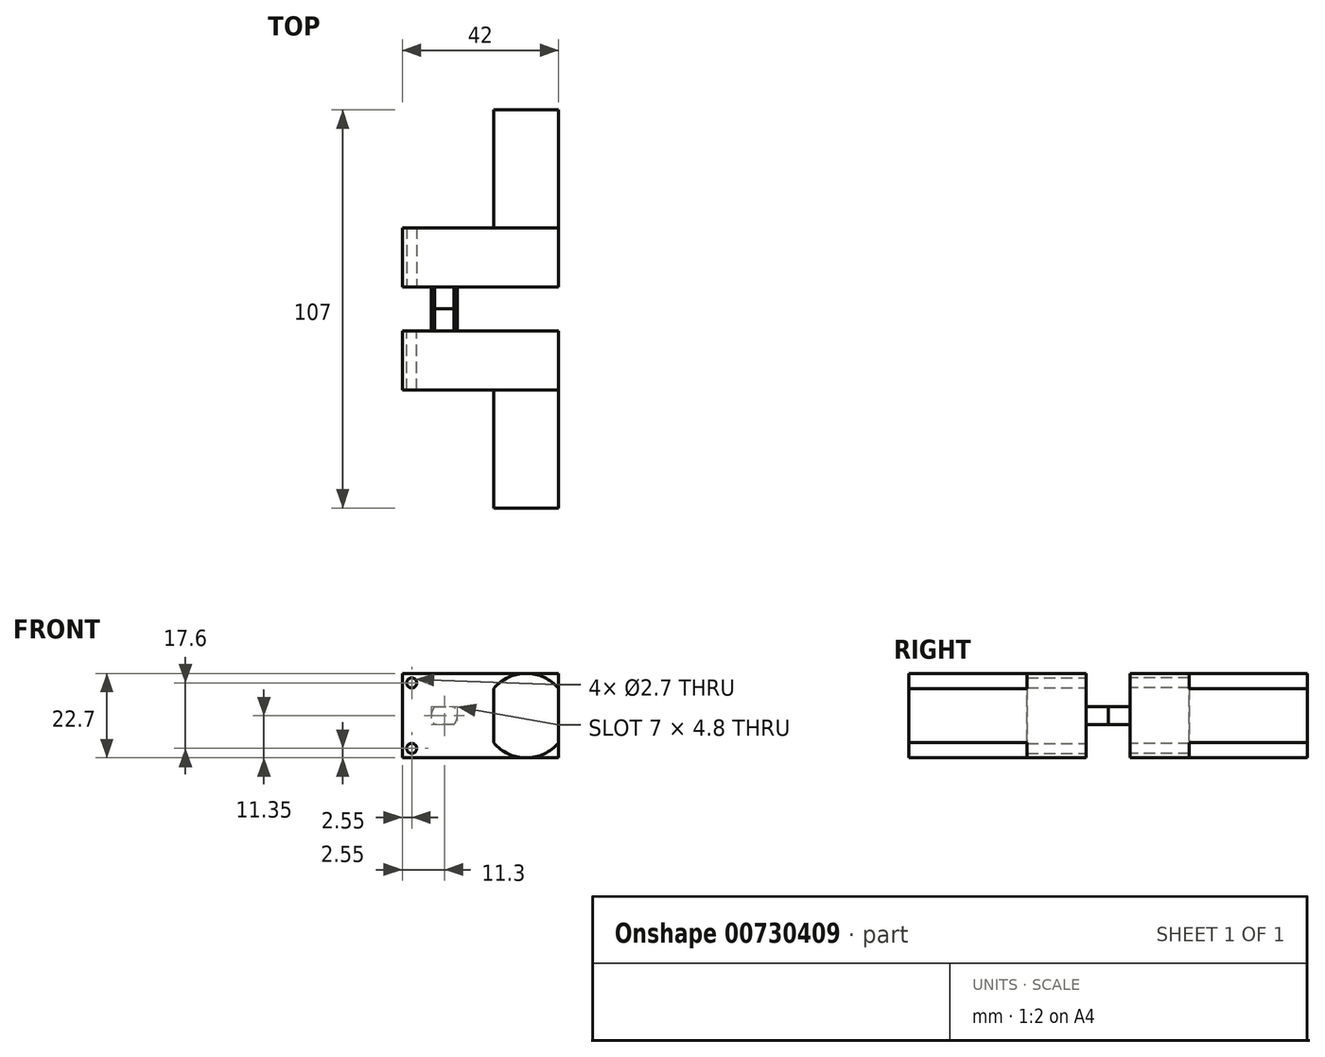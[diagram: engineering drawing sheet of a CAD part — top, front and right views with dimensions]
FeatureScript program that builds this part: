
annotation { "Feature Type Name" : "Feature", "Feature Type Description" : "" }
export const myFeature = defineFeature(function(context is Context, id is Id, definition is map)
    precondition{}
    {
        {
            var Q0;
            Q0=qCreatedBy(makeId("Front.planeOp"),FACE);
            var sketch = newSketch(context, id + "F0", { "sketchPlane" : qUnion([Q0])});
            skLineSegment(sketch, "E0.bottom", {"start": v(0, 0) * mm, "end": v(42, 0) * mm});
            skLineSegment(sketch, "E0.top", {"start": v(0, 22.7) * mm, "end": v(42, 22.7) * mm});
            skLineSegment(sketch, "E0.left", {"start": v(0, 0) * mm, "end": v(0, 22.7) * mm});
            skLineSegment(sketch, "E0.right", {"start": v(42, 0) * mm, "end": v(42, 22.7) * mm});
            skSolve(sketch);
        }
        {
            var Q0;
            Q0 = qSketchRegion(id + "F0", true);
            extrude(context, id + "F1", {"entities" : qUnion([Q0]), "depth" : 15.9 * mm, "offsetDistance" : 25 * mm});
        }
        {
            var Q0;
            Q0=makeQuery(id+"F1.opExtrude","CAP_FACE",FACE,{"disambiguationData":[OSD([sQuery(id+"F0.wireOp",EDGE,"E0.bottom"),sQuery(id+"F0.wireOp",EDGE,"E0.top"),sQuery(id+"F0.wireOp",EDGE,"E0.left"),sQuery(id+"F0.wireOp",EDGE,"E0.right")])],"isStart":false});
            var sketch = newSketch(context, id + "F2", { "sketchPlane" : qUnion([Q0])});
            skCircle(sketch, "E1", {"center": v(2.55, 20.15) * mm, "radius": 1.35 * mm});
            skCircle(sketch, "E2", {"center": v(2.55, 2.55) * mm, "radius": 1.35 * mm});
            skSolve(sketch);
        }
        {
            var Q0;
            Q0 = qSketchRegion(id + "F2", true);
            extrude(context, id + "F3", {"entities" : qUnion([Q0]), "operationType" : NewBodyOperationType.REMOVE, "endBound" : BoundingType.UP_TO_NEXT, "oppositeDirection" : true, "depth" : 25 * mm, "offsetDistance" : 25 * mm});
        }
        {
            var Q0;
            Q0=makeQuery(id+"F1.opExtrude","CAP_FACE",FACE,{"disambiguationData":[OSD([sQuery(id+"F0.wireOp",EDGE,"E0.bottom"),sQuery(id+"F0.wireOp",EDGE,"E0.top"),sQuery(id+"F0.wireOp",EDGE,"E0.left"),sQuery(id+"F0.wireOp",EDGE,"E0.right")])],"isStart":false});
            var sketch = newSketch(context, id + "F4", { "sketchPlane" : qUnion([Q0])});
            skArc(sketch, "E3", {"start": v(8.75, 13.75) * mm, "mid": v(7.8, 11.35) * mm, "end": v(8.75, 8.95) * mm});
            skPoint(sketch, "E3.centerSnap0", {"position": v(0, 11.35) * mm});
            skLineSegment(sketch, "E4", {"start": v(8.75, 13.75) * mm, "end": v(13.85, 13.75) * mm});
            skLineSegment(sketch, "E5", {"start": v(13.85, 8.95) * mm, "end": v(8.75, 8.95) * mm});
            skArc(sketch, "E6.trimOffspring", {"start": v(13.85, 8.95) * mm, "mid": v(14.8, 11.35) * mm, "end": v(13.85, 13.75) * mm});
            skSolve(sketch);
        }
        {
            var Q0;
            Q0 = qSketchRegion(id + "F4", true);
            extrude(context, id + "F5", {"entities" : qUnion([Q0]), "operationType" : NewBodyOperationType.ADD, "depth" : 5.9 * mm, "offsetDistance" : 25 * mm});
        }
        {
            var Q0;
            Q0=makeQuery(id+"F1.opExtrude","CAP_FACE",FACE,{"disambiguationData":[OSD([sQuery(id+"F0.wireOp",EDGE,"E0.bottom"),sQuery(id+"F0.wireOp",EDGE,"E0.top"),sQuery(id+"F0.wireOp",EDGE,"E0.left"),sQuery(id+"F0.wireOp",EDGE,"E0.right")])],"isStart":true});
            var sketch = newSketch(context, id + "F6", { "sketchPlane" : qUnion([Q0])});
            skArc(sketch, "E7", {"start": v(-42, 4.06) * mm, "mid": v(-33.3, 0) * mm, "end": v(-24.6, 4.06) * mm});
            skPoint(sketch, "E7.centerSnap0", {"position": v(-42, 11.35) * mm});
            skLineSegment(sketch, "E8.0", {"start": v(-42, 4.06) * mm, "end": v(-42, 18.64) * mm});
            skLineSegment(sketch, "E9", {"start": v(-24.6, 18.64) * mm, "end": v(-24.6, 4.06) * mm});
            skArc(sketch, "E10.trimOffspring", {"start": v(-24.6, 18.64) * mm, "mid": v(-33.3, 22.7) * mm, "end": v(-42, 18.64) * mm});
            skSolve(sketch);
        }
        {
            var Q0;
            Q0 = qSketchRegion(id + "F6", true);
            extrude(context, id + "F7", {"entities" : qUnion([Q0]), "operationType" : NewBodyOperationType.ADD, "depth" : 31.7 * mm, "offsetDistance" : 25 * mm});
        }
        {
            var Q0;
            Q0=makeQuery(id+"F1.opExtrude","SWEPT_BODY",BODY,{"disambiguationData":[OSD([sQuery(id+"F0.wireOp",EDGE,"E0.bottom"),sQuery(id+"F0.wireOp",EDGE,"E0.top"),sQuery(id+"F0.wireOp",EDGE,"E0.left"),sQuery(id+"F0.wireOp",EDGE,"E0.right")])]});
            var Q1;
            Q1=makeQuery(id+"F5.opExtrude","CAP_FACE",FACE,{"disambiguationData":[OSD([sQuery(id+"F4.wireOp",EDGE,"E3"),sQuery(id+"F4.wireOp",EDGE,"E4"),sQuery(id+"F4.wireOp",EDGE,"E5"),sQuery(id+"F4.wireOp",EDGE,"E6.trimOffspring")])],"isStart":false});
            mirror(context, id + "F8", {"entities" : qUnion([Q0]), "mirrorPlane" : qUnion([Q1])});
        }
    });
